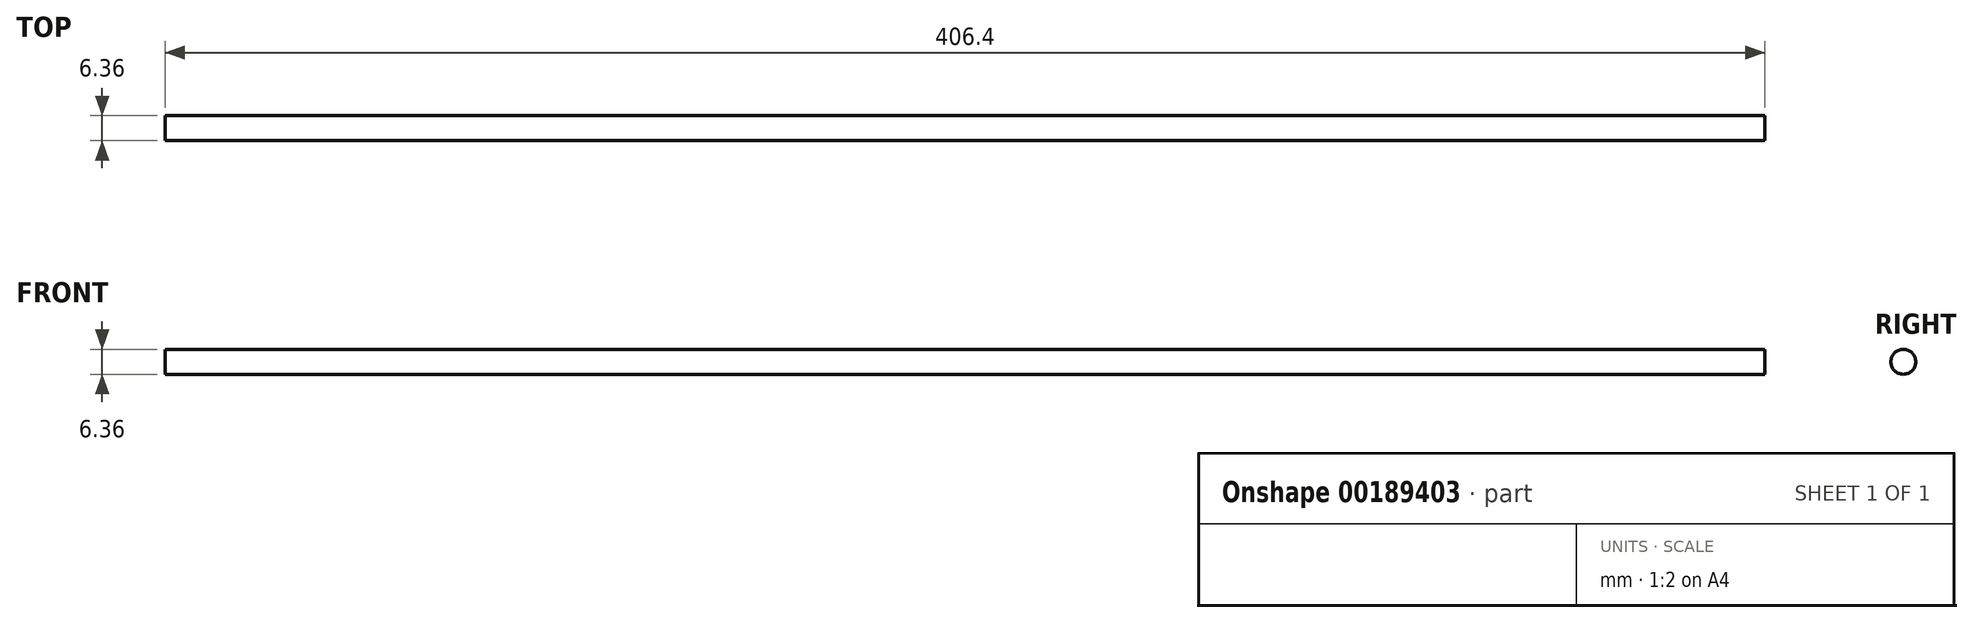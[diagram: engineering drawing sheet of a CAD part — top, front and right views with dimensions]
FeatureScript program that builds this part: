
annotation { "Feature Type Name" : "Feature", "Feature Type Description" : "" }
export const myFeature = defineFeature(function(context is Context, id is Id, definition is map)
    precondition{}
    {
        {
            var Q0;
            Q0=qCreatedBy(makeId("Right.planeOp"),FACE);
            var sketch = newSketch(context, id + "F0", { "sketchPlane" : qUnion([Q0])});
            skCircle(sketch, "E0", {"center": v(0, 0) * mm, "radius": 3.18 * mm});
            skSolve(sketch);
        }
        {
            var Q0;
            Q0=qSketchRegion(id+"F0",true);
            extrude(context, id + "F1", {"entities" : qUnion([Q0]), "depth" : 203.2 * mm, "hasSecondDirection" : true, "secondDirectionOppositeDirection" : true, "secondDirectionDepth" : 203.2 * mm});
        }
    });
